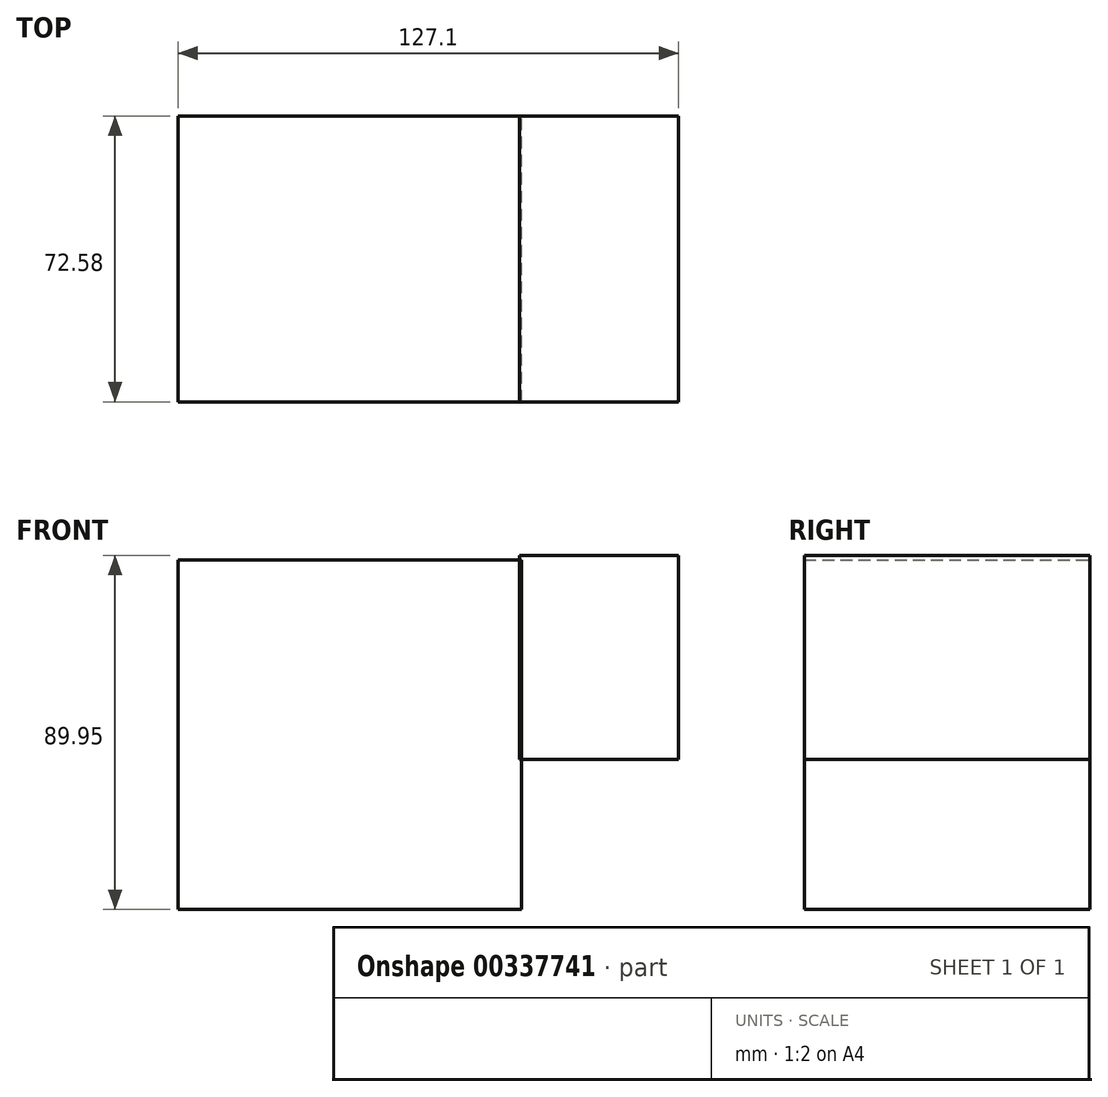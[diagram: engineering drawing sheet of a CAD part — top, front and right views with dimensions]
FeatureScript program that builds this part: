
annotation { "Feature Type Name" : "Feature", "Feature Type Description" : "" }
export const myFeature = defineFeature(function(context is Context, id is Id, definition is map)
    precondition{}
    {
        {
            var Q0;
            Q0=qCreatedBy(makeId("Front.planeOp"),FACE);
            var sketch = newSketch(context, id + "F0", { "sketchPlane" : qUnion([Q0])});
            skLineSegment(sketch, "E0.bottom", {"start": v(28.6, 50.68) * mm, "end": v(-58.66, 50.68) * mm});
            skLineSegment(sketch, "E0.top", {"start": v(28.6, -38.13) * mm, "end": v(-58.66, -38.13) * mm});
            skLineSegment(sketch, "E0.left", {"start": v(28.6, 50.68) * mm, "end": v(28.6, -38.13) * mm});
            skLineSegment(sketch, "E0.right", {"start": v(-58.66, 50.68) * mm, "end": v(-58.66, -38.13) * mm});
            skLineSegment(sketch, "E1.bottom", {"start": v(28.6, 50.68) * mm, "end": v(28.6, 50.68) * mm});
            skLineSegment(sketch, "E1.top", {"start": v(28.6, 50.68) * mm, "end": v(28.6, 50.68) * mm});
            skLineSegment(sketch, "E1.left", {"start": v(28.6, 50.68) * mm, "end": v(28.6, 50.68) * mm});
            skLineSegment(sketch, "E1.right", {"start": v(28.6, 50.68) * mm, "end": v(28.6, 50.68) * mm});
            skLineSegment(sketch, "E2.bottom", {"start": v(28.11, 51.82) * mm, "end": v(68.44, 51.82) * mm});
            skLineSegment(sketch, "E2.top", {"start": v(28.11, 0) * mm, "end": v(68.44, 0) * mm});
            skLineSegment(sketch, "E2.left", {"start": v(28.11, 51.82) * mm, "end": v(28.11, 0) * mm});
            skLineSegment(sketch, "E2.right", {"start": v(68.44, 51.82) * mm, "end": v(68.44, 0) * mm});
            skSolve(sketch);
        }
        {
            var Q0;
            {var subQ2=sQuery(id+"F0.wireOp",EDGE,"E0.top");Q0=makeQuery(id+"F0.imprint","IMPRINT",FACE,{"disambiguationData":[TD([[makeQuery(id+"F0.imprint","IMPRINT",EDGE,{"derivedFrom":subQ2}),-1.0]])]});}
            var Q1;
            {var subQ0=sQuery(id+"F0.wireOp",EDGE,"E2.bottom");Q1=makeQuery(id+"F0.imprint","IMPRINT",FACE,{"disambiguationData":[TD([[makeQuery(id+"F0.imprint","IMPRINT",EDGE,{"derivedFrom":subQ0}),-1.0]])]});}
            extrude(context, id + "F1", {"entities" : qUnion([Q0, Q1]), "depth" : 72.58 * mm});
        }
    });
